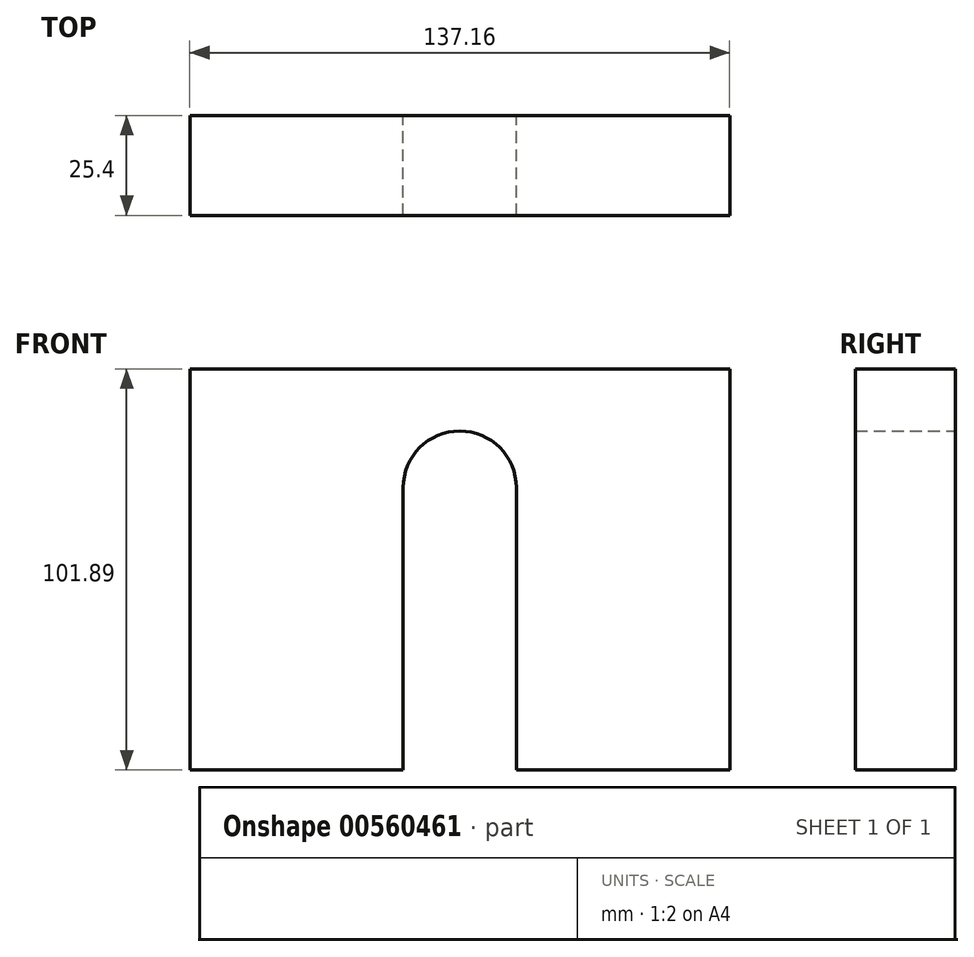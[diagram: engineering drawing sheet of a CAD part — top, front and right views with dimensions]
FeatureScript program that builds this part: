
annotation { "Feature Type Name" : "Feature", "Feature Type Description" : "" }
export const myFeature = defineFeature(function(context is Context, id is Id, definition is map)
    precondition{}
    {
        {
            var Q0;
            Q0=qCreatedBy(makeId("Front.planeOp"),FACE);
            var sketch = newSketch(context, id + "F0", { "sketchPlane" : qUnion([Q0])});
            skLineSegment(sketch, "E0.bottom", {"start": v(-20.7, -26.81) * mm, "end": v(-30.74, -26.81) * mm});
            skLineSegment(sketch, "E0.top", {"start": v(-20.7, 44.92) * mm, "end": v(-30.74, 44.92) * mm});
            skLineSegment(sketch, "E0.left", {"start": v(-20.7, -26.81) * mm, "end": v(-20.7, 44.92) * mm});
            skLineSegment(sketch, "E0.right", {"start": v(-30.74, -26.81) * mm, "end": v(-30.74, 44.92) * mm});
            skLineSegment(sketch, "E1.bottom", {"start": v(8.08, -26.81) * mm, "end": v(18.13, -26.81) * mm});
            skLineSegment(sketch, "E1.top", {"start": v(8.08, 44.92) * mm, "end": v(18.13, 44.92) * mm});
            skLineSegment(sketch, "E1.left", {"start": v(8.08, -26.81) * mm, "end": v(8.08, 44.92) * mm});
            skLineSegment(sketch, "E1.right", {"start": v(18.13, -26.81) * mm, "end": v(18.13, 44.92) * mm});
            skArc(sketch, "E2", {"start": v(8.08, 44.92) * mm, "mid": v(-6.3, 59.3) * mm, "end": v(-20.7, 44.92) * mm});
            skArc(sketch, "E3", {"start": v(18.13, 44.92) * mm, "mid": v(-6.3, 69.36) * mm, "end": v(-30.74, 44.92) * mm});
            skLineSegment(sketch, "E4", {"start": v(-30.74, -26.81) * mm, "end": v(-74.89, -26.81) * mm});
            skLineSegment(sketch, "E5", {"start": v(-74.89, -26.81) * mm, "end": v(-74.89, 75.08) * mm});
            skLineSegment(sketch, "E6", {"start": v(-74.89, 75.08) * mm, "end": v(62.27, 75.08) * mm});
            skLineSegment(sketch, "E7", {"start": v(62.27, 75.08) * mm, "end": v(62.27, -26.81) * mm});
            skLineSegment(sketch, "E8", {"start": v(62.27, -26.81) * mm, "end": v(18.13, -26.81) * mm});
            skSolve(sketch);
        }
        {
            var Q0;
            Q0=makeQuery(id+"F0.imprint","IMPRINT",FACE,{"disambiguationData":[TD([[makeQuery(id+"F0.imprint","IMPRINT",EDGE,{"derivedFrom":sQuery(id+"F0.wireOp",EDGE,"E0.top")}),-1.0]])]});
            var Q1;
            Q1=makeQuery(id+"F0.imprint","IMPRINT",FACE,{"disambiguationData":[TD([[makeQuery(id+"F0.imprint","IMPRINT",EDGE,{"derivedFrom":sQuery(id+"F0.wireOp",EDGE,"E0.bottom")}),-1.0]])]});
            var Q2;
            Q2=makeQuery(id+"F0.imprint","IMPRINT",FACE,{"disambiguationData":[TD([[makeQuery(id+"F0.imprint","IMPRINT",EDGE,{"derivedFrom":sQuery(id+"F0.wireOp",EDGE,"E1.bottom")}),1.0]])]});
            var Q3;
            Q3=makeQuery(id+"F0.imprint","IMPRINT",FACE,{"disambiguationData":[TD([[makeQuery(id+"F0.imprint","IMPRINT",EDGE,{"derivedFrom":sQuery(id+"F0.wireOp",EDGE,"E0.right")}),1.0]])]});
            extrude(context, id + "F1", {"entities" : qUnion([Q0, Q1, Q2, Q3]), "depth" : 25.4 * mm, "offsetDistance" : 25.4 * mm});
        }
    });
